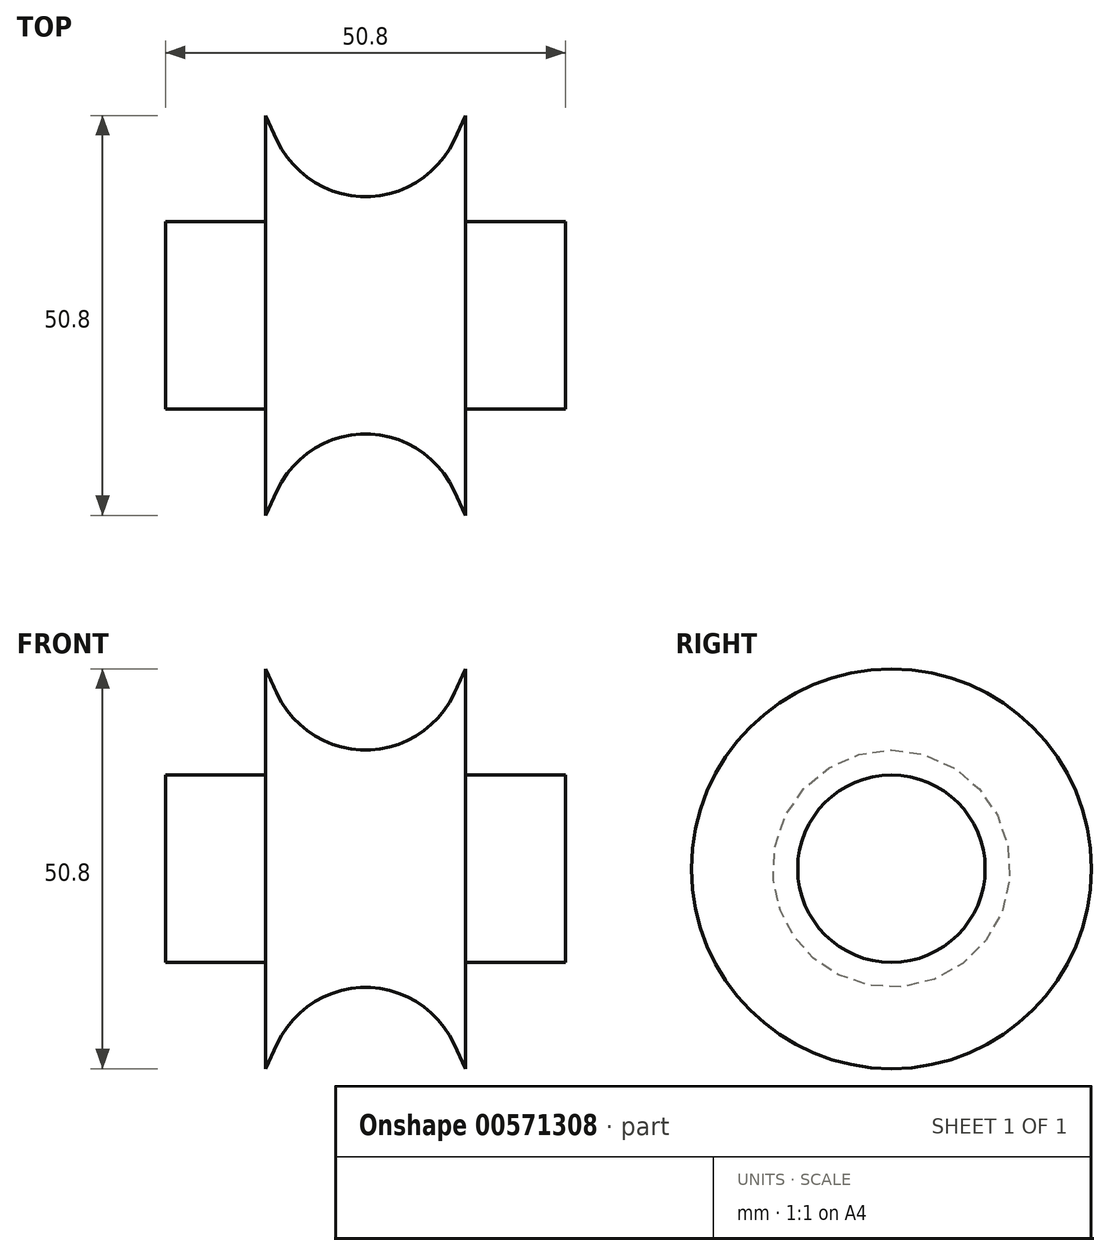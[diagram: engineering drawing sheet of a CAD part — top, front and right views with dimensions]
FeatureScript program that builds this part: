
annotation { "Feature Type Name" : "Feature", "Feature Type Description" : "" }
export const myFeature = defineFeature(function(context is Context, id is Id, definition is map)
    precondition{}
    {
        {
            var Q0;
            Q0=qCreatedBy(makeId("Front.planeOp"),FACE);
            var sketch = newSketch(context, id + "F0", { "sketchPlane" : qUnion([Q0])});
            skLineSegment(sketch, "E0", {"start": v(-25.4, 0) * mm, "end": v(-25.4, 11.9) * mm});
            skLineSegment(sketch, "E1", {"start": v(0, 0) * mm, "end": v(-25.4, 0) * mm});
            skLineSegment(sketch, "E2", {"start": v(-25.4, 11.9) * mm, "end": v(-12.7, 11.9) * mm});
            skLineSegment(sketch, "E3", {"start": v(-12.7, 11.9) * mm, "end": v(-12.7, 25.4) * mm});
            skLineSegment(sketch, "E4.MirrorCS", {"start": v(12.7, 11.9) * mm, "end": v(12.7, 25.4) * mm});
            skLineSegment(sketch, "E5.MirrorCS", {"start": v(25.4, 11.9) * mm, "end": v(12.7, 11.9) * mm});
            skLineSegment(sketch, "E6.MirrorCS", {"start": v(25.4, 0) * mm, "end": v(25.4, 11.9) * mm});
            skLineSegment(sketch, "E7.MirrorCS", {"start": v(0, 0) * mm, "end": v(25.4, 0) * mm});
            skLineSegment(sketch, "E8", {"start": v(-12.7, 25.4) * mm, "end": v(-11.22, 22.22) * mm});
            skLineSegment(sketch, "E9.MirrorCS", {"start": v(12.7, 25.4) * mm, "end": v(11.22, 22.22) * mm});
            skArc(sketch, "E10", {"start": v(-11.22, 22.22) * mm, "mid": v(0, 15.08) * mm, "end": v(11.22, 22.22) * mm});
            skLineSegment(sketch, "E11", {"start": v(-42.62, 0) * mm, "end": v(31.46, 0) * mm, "construction": true});
            skSolve(sketch);
        }
        {
            var Q0;
            Q0=makeQuery(id+"F0.imprint","IMPRINT",FACE,{"disambiguationData":[TD([[makeQuery(id+"F0.imprint","IMPRINT",EDGE,{"derivedFrom":sQuery(id+"F0.wireOp",EDGE,"E0")}),-1.0]])]});
            var Q1;
            Q1=sQuery(id+"F0.wireOp",EDGE,"E11");
            revolve(context, id + "F1", {"entities" : qUnion([Q0]), "axis" : qUnion([Q1]), "revolveType" : RevolveType.FULL});
        }
    });
